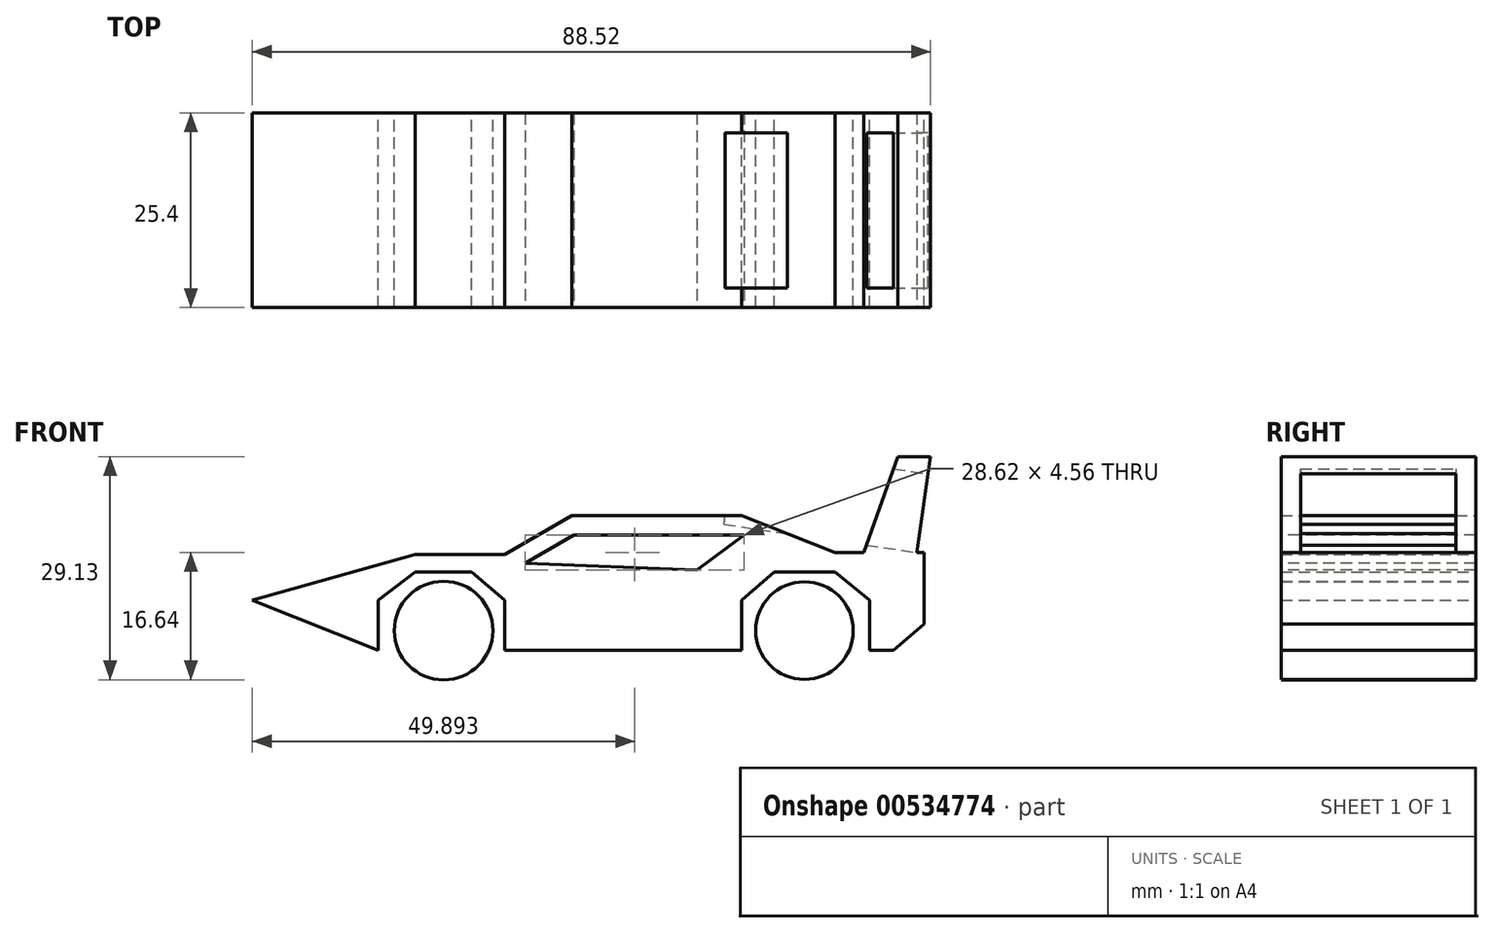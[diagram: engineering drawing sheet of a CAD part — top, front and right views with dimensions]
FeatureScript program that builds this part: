
annotation { "Feature Type Name" : "Feature", "Feature Type Description" : "" }
export const myFeature = defineFeature(function(context is Context, id is Id, definition is map)
    precondition{}
    {
        {
            var Q0;
            Q0=qCreatedBy(makeId("Front.planeOp"),FACE);
            var sketch = newSketch(context, id + "F0", { "sketchPlane" : qUnion([Q0])});
            skCircle(sketch, "E0", {"center": v(-33.05, 5.67) * mm, "radius": 6.43 * mm});
            skCircle(sketch, "E1", {"center": v(14.04, 5.67) * mm, "radius": 6.38 * mm});
            skSolve(sketch);
        }
        {
            var Q0;
            Q0=makeQuery(id+"F0.imprint","IMPRINT",FACE,{"disambiguationData":[TD([[makeQuery(id+"F0.imprint","IMPRINT",EDGE,{"derivedFrom":sQuery(id+"F0.wireOp",EDGE,"E0")}),1.0]])]});
            var Q1;
            Q1=makeQuery(id+"F0.imprint","IMPRINT",FACE,{"disambiguationData":[TD([[makeQuery(id+"F0.imprint","IMPRINT",EDGE,{"derivedFrom":sQuery(id+"F0.wireOp",EDGE,"E1")}),1.0]])]});
            extrude(context, id + "F1", {"entities" : qUnion([Q0, Q1]), "depth" : 25.4 * mm, "offsetDistance" : 25.4 * mm});
        }
        {
            var Q0;
            Q0=qCreatedBy(makeId("Front.planeOp"),FACE);
            var sketch = newSketch(context, id + "F2", { "sketchPlane" : qUnion([Q0])});
            skLineSegment(sketch, "E2", {"start": v(-25.1, 3.12) * mm, "end": v(5.82, 3.12) * mm});
            skLineSegment(sketch, "E3", {"start": v(-25.1, 3.12) * mm, "end": v(-25.1, 9.65) * mm});
            skLineSegment(sketch, "E4", {"start": v(-25.1, 9.65) * mm, "end": v(-29.37, 13.34) * mm});
            skLineSegment(sketch, "E5", {"start": v(-29.37, 13.34) * mm, "end": v(-36.74, 13.34) * mm});
            skLineSegment(sketch, "E6", {"start": v(-36.74, 13.34) * mm, "end": v(-41.57, 9.65) * mm});
            skLineSegment(sketch, "E7", {"start": v(-41.57, 9.65) * mm, "end": v(-41.57, 3.12) * mm});
            skLineSegment(sketch, "E8", {"start": v(-41.57, 3.12) * mm, "end": v(-58.02, 9.65) * mm});
            skLineSegment(sketch, "E9", {"start": v(-58.02, 9.65) * mm, "end": v(-36.74, 15.6) * mm});
            skLineSegment(sketch, "E10", {"start": v(-36.74, 15.6) * mm, "end": v(-25.1, 15.6) * mm});
            skLineSegment(sketch, "E11", {"start": v(-25.1, 15.6) * mm, "end": v(-16.31, 20.71) * mm});
            skLineSegment(sketch, "E12", {"start": v(-16.31, 20.71) * mm, "end": v(5.82, 20.71) * mm});
            skLineSegment(sketch, "E13", {"start": v(5.82, 20.71) * mm, "end": v(18, 15.88) * mm});
            skLineSegment(sketch, "E14", {"start": v(18, 15.88) * mm, "end": v(29.65, 15.88) * mm});
            skLineSegment(sketch, "E15", {"start": v(29.65, 15.88) * mm, "end": v(29.65, 6.53) * mm});
            skLineSegment(sketch, "E16", {"start": v(29.65, 6.53) * mm, "end": v(25.68, 3.12) * mm});
            skLineSegment(sketch, "E17", {"start": v(25.68, 3.12) * mm, "end": v(22.56, 3.12) * mm});
            skLineSegment(sketch, "E18", {"start": v(22.56, 3.12) * mm, "end": v(22.56, 9.65) * mm});
            skLineSegment(sketch, "E19", {"start": v(22.56, 9.65) * mm, "end": v(18, 13.34) * mm});
            skLineSegment(sketch, "E20", {"start": v(18, 13.34) * mm, "end": v(10.07, 13.34) * mm});
            skLineSegment(sketch, "E21", {"start": v(10.07, 13.34) * mm, "end": v(5.82, 9.65) * mm});
            skLineSegment(sketch, "E22", {"start": v(5.82, 9.65) * mm, "end": v(5.82, 3.12) * mm});
            skSolve(sketch);
        }
        {
            var Q0;
            Q0=makeQuery(id+"F2.imprint","IMPRINT",FACE,{"disambiguationData":[TD([[makeQuery(id+"F2.imprint","IMPRINT",EDGE,{"derivedFrom":sQuery(id+"F2.wireOp",EDGE,"E2")}),1.0]])]});
            extrude(context, id + "F3", {"entities" : qUnion([Q0]), "depth" : 25.4 * mm, "offsetDistance" : 25.4 * mm});
        }
        {
            var Q0;
            Q0=qCreatedBy(makeId("Front.planeOp"),FACE);
            var sketch = newSketch(context, id + "F4", { "sketchPlane" : qUnion([Q0])});
            skLineSegment(sketch, "E23", {"start": v(28.51, 14.75) * mm, "end": v(30.5, 28.37) * mm});
            skLineSegment(sketch, "E24", {"start": v(30.5, 28.37) * mm, "end": v(26.24, 28.37) * mm});
            skLineSegment(sketch, "E25", {"start": v(26.24, 28.37) * mm, "end": v(21.7, 15.6) * mm});
            skLineSegment(sketch, "E26", {"start": v(21.7, 15.6) * mm, "end": v(28.51, 14.75) * mm});
            skSolve(sketch);
        }
        {
            var Q0;
            Q0=makeQuery(id+"F4.imprint","IMPRINT",FACE,{"disambiguationData":[TD([[makeQuery(id+"F4.imprint","IMPRINT",EDGE,{"derivedFrom":sQuery(id+"F4.wireOp",EDGE,"E23")}),1.0]])]});
            extrude(context, id + "F5", {"entities" : qUnion([Q0]), "operationType" : NewBodyOperationType.ADD, "depth" : 25.4 * mm, "offsetDistance" : 25.4 * mm});
        }
        {
            var Q0;
            Q0=qCreatedBy(makeId("Front.planeOp"),FACE);
            var sketch = newSketch(context, id + "F6", { "sketchPlane" : qUnion([Q0])});
            skLineSegment(sketch, "E27", {"start": v(-19.44, 14.75) * mm, "end": v(-14.9, 17.87) * mm});
            skLineSegment(sketch, "E28", {"start": v(-14.9, 17.87) * mm, "end": v(5.25, 17.87) * mm});
            skLineSegment(sketch, "E29", {"start": v(5.25, 17.87) * mm, "end": v(5.25, 14.75) * mm});
            skLineSegment(sketch, "E30", {"start": v(5.25, 14.75) * mm, "end": v(-19.44, 14.75) * mm});
            skSolve(sketch);
        }
        {
            var Q0;
            Q0=makeQuery(id+"F6.imprint","IMPRINT",FACE,{"disambiguationData":[TD([[makeQuery(id+"F6.imprint","IMPRINT",EDGE,{"derivedFrom":sQuery(id+"F6.wireOp",EDGE,"E27")}),-1.0]])]});
            extrude(context, id + "F7", {"entities" : qUnion([Q0]), "operationType" : NewBodyOperationType.REMOVE, "oppositeDirection" : true, "depth" : 22.86 * mm, "offsetDistance" : 25.4 * mm});
        }
        {
            var Q0;
            Q0=makeQuery(id+"F5.opExtrude","SWEPT_FACE",FACE,{"disambiguationData":[OSD([sQuery(id+"F4.wireOp",EDGE,"E23")])]});
            var sketch = newSketch(context, id + "F8", { "sketchPlane" : qUnion([Q0])});
            skLineSegment(sketch, "E31", {"start": v(-22.85, 19.85) * mm, "end": v(-22.85, 30.22) * mm});
            skLineSegment(sketch, "E32", {"start": v(-22.85, 30.22) * mm, "end": v(-2.6, 30.22) * mm});
            skLineSegment(sketch, "E33", {"start": v(-2.6, 30.22) * mm, "end": v(-2.6, 19.85) * mm});
            skLineSegment(sketch, "E34", {"start": v(-2.6, 19.85) * mm, "end": v(-22.85, 19.85) * mm});
            skSolve(sketch);
        }
        {
            var Q0;
            Q0=makeQuery(id+"F8.imprint","IMPRINT",FACE,{"disambiguationData":[TD([[makeQuery(id+"F8.imprint","IMPRINT",EDGE,{"derivedFrom":sQuery(id+"F8.wireOp",EDGE,"E31")}),-1.0]])]});
            extrude(context, id + "F9", {"entities" : qUnion([Q0]), "operationType" : NewBodyOperationType.REMOVE, "oppositeDirection" : true, "depth" : 25.4 * mm, "offsetDistance" : 25.4 * mm});
        }
        {
            var Q0;
            Q0=makeQuery(id+"F5.boolean.opBoolean","MERGE",FACE,{"derivedFrom":[makeQuery(id+"F3.opExtrude","CAP_FACE",FACE,{"disambiguationData":[OSD([sQuery(id+"F2.wireOp",EDGE,"E2"),sQuery(id+"F2.wireOp",EDGE,"E3"),sQuery(id+"F2.wireOp",EDGE,"E4"),sQuery(id+"F2.wireOp",EDGE,"E5"),sQuery(id+"F2.wireOp",EDGE,"E6"),sQuery(id+"F2.wireOp",EDGE,"E7"),sQuery(id+"F2.wireOp",EDGE,"E8"),sQuery(id+"F2.wireOp",EDGE,"E9"),sQuery(id+"F2.wireOp",EDGE,"E10"),sQuery(id+"F2.wireOp",EDGE,"E11"),sQuery(id+"F2.wireOp",EDGE,"E12"),sQuery(id+"F2.wireOp",EDGE,"E13"),sQuery(id+"F2.wireOp",EDGE,"E14"),sQuery(id+"F2.wireOp",EDGE,"E15"),sQuery(id+"F2.wireOp",EDGE,"E16"),sQuery(id+"F2.wireOp",EDGE,"E17"),sQuery(id+"F2.wireOp",EDGE,"E18"),sQuery(id+"F2.wireOp",EDGE,"E19"),sQuery(id+"F2.wireOp",EDGE,"E20"),sQuery(id+"F2.wireOp",EDGE,"E21"),sQuery(id+"F2.wireOp",EDGE,"E22")])],"isStart":false}),makeQuery(id+"F5.opExtrude","CAP_FACE",FACE,{"disambiguationData":[OSD([sQuery(id+"F4.wireOp",EDGE,"E23"),sQuery(id+"F4.wireOp",EDGE,"E24"),sQuery(id+"F4.wireOp",EDGE,"E25"),sQuery(id+"F4.wireOp",EDGE,"E26")])],"isStart":false})]});
            var sketch = newSketch(context, id + "F10", { "sketchPlane" : qUnion([Q0])});
            skLineSegment(sketch, "E35", {"start": v(-22.44, 14.44) * mm, "end": v(-16.04, 18.16) * mm});
            skPoint(sketch, "E35.endSnap0", {"position": v(-20.71, 18.16) * mm});
            skLineSegment(sketch, "E36", {"start": v(-16.04, 18.16) * mm, "end": v(6.18, 18.16) * mm});
            skLineSegment(sketch, "E37", {"start": v(6.18, 18.16) * mm, "end": v(0, 13.6) * mm});
            skLineSegment(sketch, "E38", {"start": v(0, 13.6) * mm, "end": v(-22.44, 14.44) * mm});
            skSolve(sketch);
        }
        {
            var Q0;
            Q0=makeQuery(id+"F10.imprint","IMPRINT",FACE,{"disambiguationData":[TD([[makeQuery(id+"F10.imprint","IMPRINT",EDGE,{"derivedFrom":sQuery(id+"F10.wireOp",EDGE,"E35")}),-1.0]])]});
            extrude(context, id + "F11", {"entities" : qUnion([Q0]), "operationType" : NewBodyOperationType.REMOVE, "oppositeDirection" : true, "depth" : 25.4 * mm, "offsetDistance" : 25.4 * mm});
        }
    });
